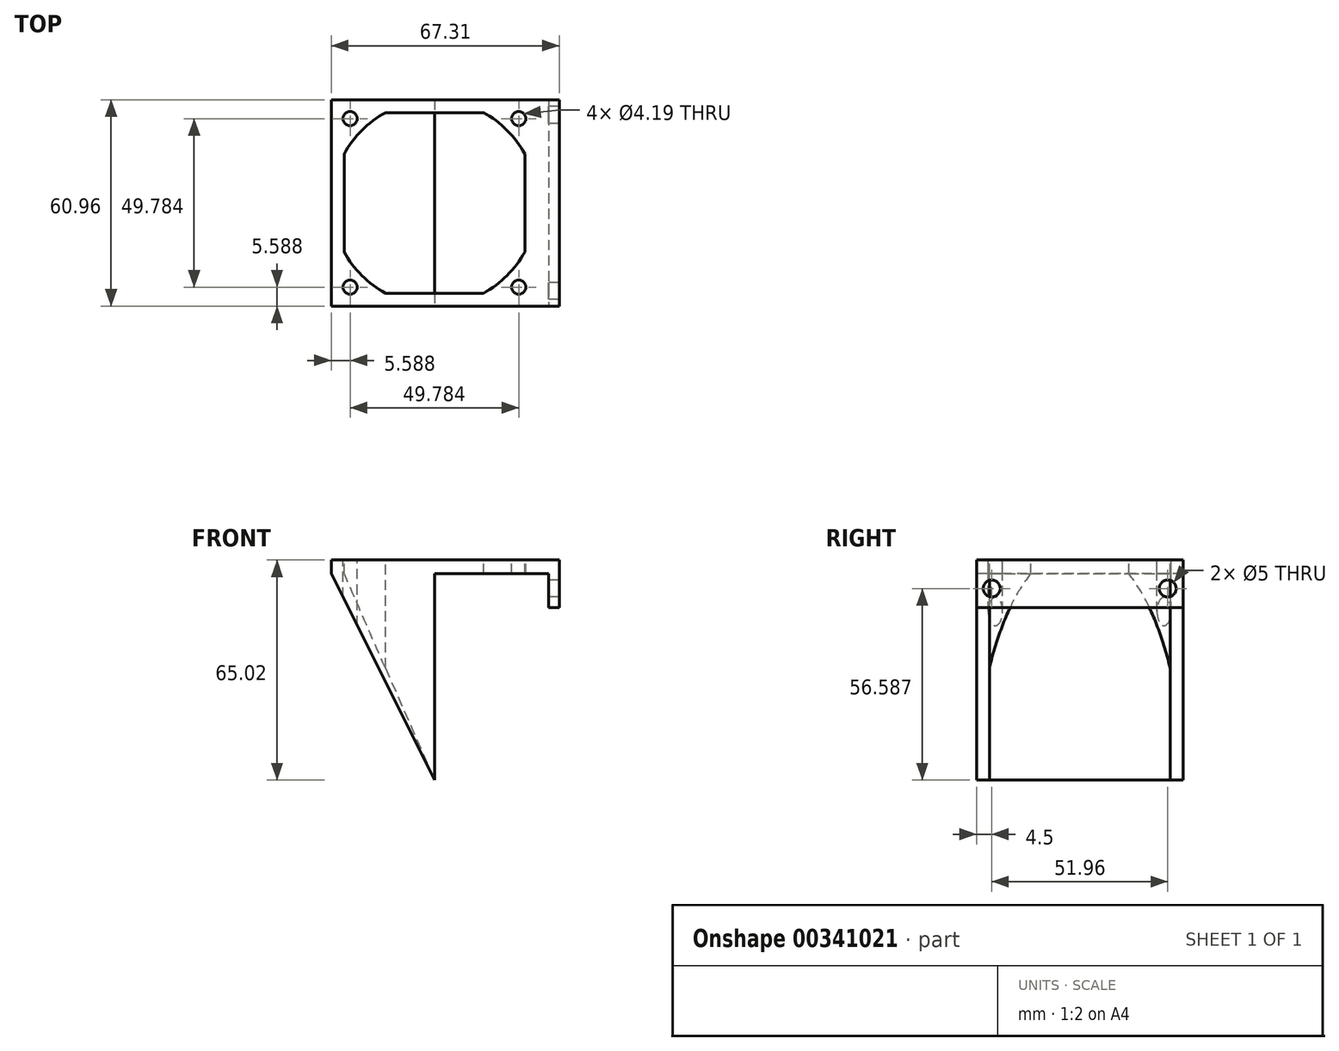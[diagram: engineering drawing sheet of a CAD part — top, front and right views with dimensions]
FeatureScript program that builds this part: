
annotation { "Feature Type Name" : "Feature", "Feature Type Description" : "" }
export const myFeature = defineFeature(function(context is Context, id is Id, definition is map)
    precondition{}
    {
        {
            var Q0;
            Q0=qCreatedBy(makeId("Right.planeOp"),FACE);
            var sketch = newSketch(context, id + "F0", { "sketchPlane" : qUnion([Q0])});
            skLineSegment(sketch, "E0.bottom", {"start": v(-27.89, 24.57) * mm, "end": v(33.07, 24.57) * mm});
            skLineSegment(sketch, "E0.top", {"start": v(-27.89, 20.5) * mm, "end": v(33.07, 20.5) * mm});
            skLineSegment(sketch, "E0.left", {"start": v(-27.89, 24.57) * mm, "end": v(-27.89, 20.5) * mm});
            skLineSegment(sketch, "E0.right", {"start": v(33.07, 24.57) * mm, "end": v(33.07, 20.5) * mm});
            skSolve(sketch);
        }
        {
            var Q0;
            Q0=qSketchRegion(id+"F0",true);
            extrude(context, id + "F1", {"entities" : qUnion([Q0]), "depth" : 60.96 * mm});
        }
        {
            var Q0;
            Q0=makeQuery(id+"F1.opExtrude","SWEPT_FACE",FACE,{"disambiguationData":[OSD([sQuery(id+"F0.wireOp",EDGE,"E0.bottom")])]});
            var sketch = newSketch(context, id + "F2", { "sketchPlane" : qUnion([Q0])});
            skLineSegment(sketch, "E1.bottom", {"start": v(44.96, -24.08) * mm, "end": v(16, -24.08) * mm});
            skLineSegment(sketch, "E1.top", {"start": v(44.96, 29.26) * mm, "end": v(16, 29.26) * mm});
            skLineSegment(sketch, "E1.left", {"start": v(57.15, -11.89) * mm, "end": v(57.15, 17.07) * mm});
            skLineSegment(sketch, "E1.right", {"start": v(3.81, -11.89) * mm, "end": v(3.81, 17.07) * mm});
            skArc(sketch, "E2", {"start": v(3.8, -11.89) * mm, "mid": v(9.03, -18.86) * mm, "end": v(16, -24.08) * mm});
            skArc(sketch, "E3", {"start": v(16, 29.26) * mm, "mid": v(9.04, 24.03) * mm, "end": v(3.8, 17.07) * mm});
            skArc(sketch, "E4", {"start": v(57.15, 17.07) * mm, "mid": v(51.93, 24.04) * mm, "end": v(44.96, 29.26) * mm});
            skArc(sketch, "E5", {"start": v(44.96, -24.08) * mm, "mid": v(51.93, -18.86) * mm, "end": v(57.15, -11.89) * mm});
            skPoint(sketch, "E6.orphan", {"position": v(3.81, -24.08) * mm});
            skPoint(sketch, "E7.orphan", {"position": v(3.81, 29.26) * mm});
            skPoint(sketch, "E8.orphan", {"position": v(57.15, 29.26) * mm});
            skPoint(sketch, "E9.orphan", {"position": v(57.15, -24.08) * mm});
            skSolve(sketch);
        }
        {
            var Q0;
            Q0=qSketchRegion(id+"F2",true);
            extrude(context, id + "F3", {"entities" : qUnion([Q0]), "operationType" : NewBodyOperationType.REMOVE, "oppositeDirection" : true, "depth" : 25.4 * mm});
        }
        {
            var Q0;
            Q0=makeQuery(id+"F1.opExtrude","SWEPT_FACE",FACE,{"disambiguationData":[OSD([sQuery(id+"F0.wireOp",EDGE,"E0.bottom")])]});
            var sketch = newSketch(context, id + "F4", { "sketchPlane" : qUnion([Q0])});
            skCircle(sketch, "E10", {"center": v(55.37, -22.3) * mm, "radius": 2.1 * mm});
            skCircle(sketch, "E11", {"center": v(55.37, 27.48) * mm, "radius": 2.1 * mm});
            skCircle(sketch, "E12", {"center": v(5.59, -22.3) * mm, "radius": 2.1 * mm});
            skCircle(sketch, "E13", {"center": v(5.59, 27.48) * mm, "radius": 2.1 * mm});
            skSolve(sketch);
        }
        {
            var Q0;
            Q0=makeQuery(id+"F1.opExtrude","SWEPT_FACE",FACE,{"disambiguationData":[OSD([sQuery(id+"F0.wireOp",EDGE,"E0.left")])]});
            var sketch = newSketch(context, id + "F5", { "sketchPlane" : qUnion([Q0])});
            skLineSegment(sketch, "E14", {"start": v(30.48, 20.5) * mm, "end": v(30.48, -40.45) * mm});
            skLineSegment(sketch, "E15", {"start": v(30.48, -40.45) * mm, "end": v(0, 20.5) * mm});
            skLineSegment(sketch, "E16", {"start": v(0, 20.5) * mm, "end": v(30.48, 20.5) * mm});
            skSolve(sketch);
        }
        {
            var Q0;
            Q0=qSketchRegion(id+"F5",true);
            extrude(context, id + "F6", {"entities" : qUnion([Q0]), "operationType" : NewBodyOperationType.ADD, "oppositeDirection" : true, "depth" : 60.96 * mm});
        }
        {
            var Q0;
            {var subQ0=sQuery(id+"F5.wireOp",EDGE,"E14");var subQ1=sQuery(id+"F5.wireOp",EDGE,"E16");Q0=makeQuery(id+"F6.boolean.opBoolean","SPLIT",EDGE,{"disambiguationData":[topologyDisambiguationEdgeConnected([makeQuery(id+"F6.opExtrude","SWEPT_FACE",FACE,{"disambiguationData":[OSD([subQ0])]}),makeQuery(id+"F6.opExtrude","SWEPT_FACE",FACE,{"disambiguationData":[OSD([subQ1])]})])],"derivedFrom":makeQuery(id+"F6.opExtrude","SWEPT_EDGE",EDGE,{"disambiguationData":[OSD([sQuery(id+"F0.wireOp",EDGE,"E0.top"),sQuery(id+"F0.wireOp",EDGE,"E0.left"),subQ0,subQ1])]})});}
            chamfer(context, id + "F7", {"entities" : qUnion([Q0]), "chamferType" : ChamferType.TWO_OFFSETS, "width1" : 60.96 * mm, "oppositeDirection" : false, "width2" : 26.67 * mm, "tangentPropagation" : true});
        }
        {
            var Q0;
            Q0=makeQuery(id+"F1.opExtrude","CAP_FACE",FACE,{"disambiguationData":[OSD([sQuery(id+"F0.wireOp",EDGE,"E0.bottom"),sQuery(id+"F0.wireOp",EDGE,"E0.top"),sQuery(id+"F0.wireOp",EDGE,"E0.left"),sQuery(id+"F0.wireOp",EDGE,"E0.right")])],"isStart":false});
            var sketch = newSketch(context, id + "F8", { "sketchPlane" : qUnion([Q0])});
            skLineSegment(sketch, "E17.bottom", {"start": v(-27.89, 24.57) * mm, "end": v(33.07, 24.57) * mm});
            skLineSegment(sketch, "E17.top", {"start": v(-27.89, 20.5) * mm, "end": v(33.07, 20.5) * mm});
            skLineSegment(sketch, "E17.left", {"start": v(-27.89, 24.57) * mm, "end": v(-27.89, 20.5) * mm});
            skLineSegment(sketch, "E17.right", {"start": v(33.07, 24.57) * mm, "end": v(33.07, 20.5) * mm});
            skSolve(sketch);
        }
        {
            var Q0;
            Q0=qSketchRegion(id+"F8",true);
            extrude(context, id + "F9", {"entities" : qUnion([Q0]), "operationType" : NewBodyOperationType.ADD, "depth" : 6.35 * mm});
        }
        {
            var Q0;
            Q0=makeQuery(id+"F9.boolean.opBoolean","MERGE",FACE,{"derivedFrom":[makeQuery(id+"F1.opExtrude","SWEPT_FACE",FACE,{"disambiguationData":[OSD([sQuery(id+"F0.wireOp",EDGE,"E0.top")])]}),makeQuery(id+"F9.opExtrude","SWEPT_FACE",FACE,{"disambiguationData":[OSD([sQuery(id+"F8.wireOp",EDGE,"E17.top")])]})]});
            var sketch = newSketch(context, id + "F10", { "sketchPlane" : qUnion([Q0])});
            skLineSegment(sketch, "E18.bottom", {"start": v(67.3, -33.07) * mm, "end": v(64.13, -33.07) * mm});
            skLineSegment(sketch, "E18.top", {"start": v(67.3, 27.89) * mm, "end": v(64.13, 27.89) * mm});
            skLineSegment(sketch, "E18.left", {"start": v(67.3, -33.07) * mm, "end": v(67.3, 27.89) * mm});
            skLineSegment(sketch, "E18.right", {"start": v(64.13, -33.07) * mm, "end": v(64.13, 27.89) * mm});
            skSolve(sketch);
        }
        {
            var Q0;
            Q0=qSketchRegion(id+"F10",true);
            extrude(context, id + "F11", {"entities" : qUnion([Q0]), "operationType" : NewBodyOperationType.ADD, "depth" : 10 * mm});
        }
        {
            var Q0;
            Q0=makeQuery(id+"F11.opExtrude","SWEPT_FACE",FACE,{"disambiguationData":[OSD([sQuery(id+"F10.wireOp",EDGE,"E18.right")])]});
            var sketch = newSketch(context, id + "F12", { "sketchPlane" : qUnion([Q0])});
            skCircle(sketch, "E19", {"center": v(-28.57, 16.14) * mm, "radius": 2.5 * mm});
            skSolve(sketch);
        }
        {
            var Q0;
            Q0=makeQuery(id+"F11.opExtrude","SWEPT_FACE",FACE,{"disambiguationData":[OSD([sQuery(id+"F10.wireOp",EDGE,"E18.right")])]});
            var sketch = newSketch(context, id + "F13", { "sketchPlane" : qUnion([Q0])});
            skCircle(sketch, "E20", {"center": v(23.39, 16.14) * mm, "radius": 2.5 * mm});
            skSolve(sketch);
        }
        {
            var Q0;
            Q0 = qSketchRegion(id + "F4", true);
            extrude(context, id + "F14", {"entities" : qUnion([Q0]), "operationType" : NewBodyOperationType.REMOVE, "endBound" : BoundingType.THROUGH_ALL, "oppositeDirection" : true, "depth" : 25.4 * mm});
        }
        {
            var Q0;
            Q0 = qSketchRegion(id + "F13", true);
            extrude(context, id + "F15", {"entities" : qUnion([Q0]), "operationType" : NewBodyOperationType.REMOVE, "oppositeDirection" : true, "depth" : 25.4 * mm});
        }
        {
            var Q0;
            Q0 = qSketchRegion(id + "F12", true);
            extrude(context, id + "F16", {"entities" : qUnion([Q0]), "operationType" : NewBodyOperationType.REMOVE, "oppositeDirection" : true, "depth" : 25.4 * mm});
        }
    });
